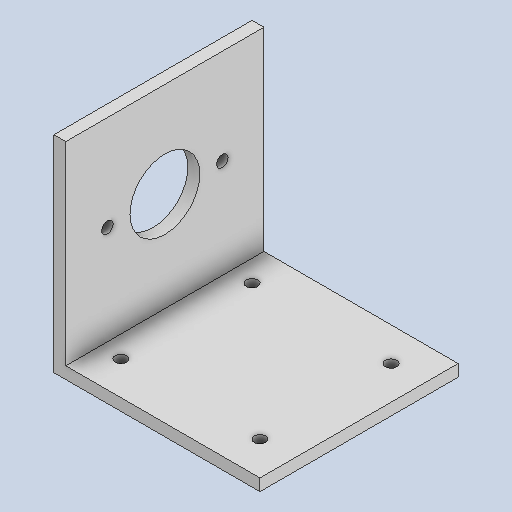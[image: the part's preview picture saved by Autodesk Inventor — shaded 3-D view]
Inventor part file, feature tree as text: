
AUTODESK INVENTOR PART (.ipt)
format: ipt  version: 2022 (Build 260153000, 153)  size: 148,992 bytes
history: native  units: mm
features: extrude x3, sketch x3
ambient origin geometry x8: Origin, YZ Plane, XZ Plane, XY Plane, X Axis, Y Axis, Z Axis, Center Point
bodies: Solid1 (feature_tree)
feature tree (6):
  extrude  "Extrusion1"  Depth=3.0mm
  extrude  "Extrusion2"  Depth=52.0mm
  extrude  "Extrusion3"  Depth=50.0mm
  sketch  "Sketch1"  dims[d0=3.0mm d1=3.0mm]
  sketch  "Sketch2"  dims[d2=52.0mm d3=52.0mm]
  sketch  "Sketch3"  dims[d4=50.0mm d5=0.0mm d6=17.6mm d7=24.0mm d8=25.0mm d9=2.903mm d10=2.903mm d11=29.0mm d12=14.5mm d13=14.5mm d14=0.0mm d15=0.0mm d16=2.903mm d17=2.903mm d18=2.903mm d19=2.903mm d20=7.0mm d21=7.0mm d22=7.0mm d23=7.0mm d24=7.0mm d25=7.0mm d26=7.0mm d27=7.0mm d28=0.0mm d29=0.0mm]
